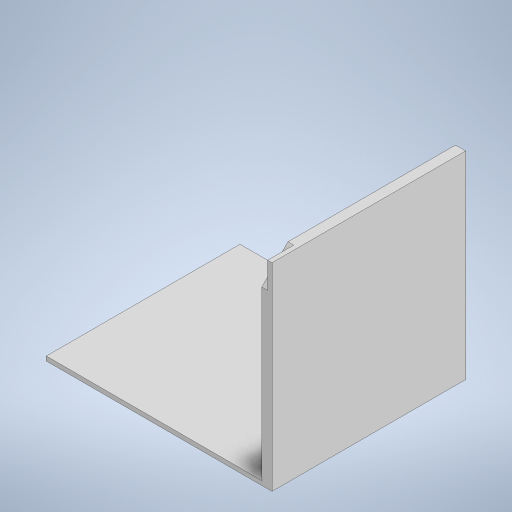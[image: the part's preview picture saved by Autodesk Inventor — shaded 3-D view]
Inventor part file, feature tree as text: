
AUTODESK INVENTOR PART (.ipt)
format: ipt  version: 2024 (Build 280153000, 153)  size: 322,048 bytes
history: native  units: mm
features: extrude x11, sketch x11
ambient origin geometry x8: Origin, YZ Plane, XZ Plane, XY Plane, X Axis, Y Axis, Z Axis, Center Point
bodies: Solid1 (feature_tree)
feature tree (22):
  extrude  "Top"  Depth=160.0mm
  extrude  "Right"  Depth=179.5mm
  extrude  "Left"  Depth=215.9mm
  extrude  "Plexiglass Cut"  Depth=25.4mm
  extrude  "Bottom"  Depth=266.7mm TaperAngle=0.0deg
  extrude  "Top Flattening"  Depth=266.7mm TaperAngle=0.0deg
  extrude  "Outer Side Flattening"  Depth=304.8mm TaperAngle=0.0deg
  extrude  "Bottom Flattening"  Depth=22.4mm TaperAngle=0.0deg
  extrude  "Inner Flattening"  Depth=22.389425mm
  extrude  "Top Cut"  Depth=22.4mm TaperAngle=0.0deg
  extrude  "Quarter Cut"  Depth=22.4mm TaperAngle=0.0deg
  sketch  "Sketch1"  dims[d11=220.0mm d12=160.0mm]
  sketch  "Sketch3"  dims[d15=248.6mm d16=179.5mm]
  sketch  "Sketch4"  dims[d18=304.8mm d19=215.9mm]
  sketch  "Sketch5"  dims[d20=25.4mm d21=0.0mm d22=25.4mm]
  sketch  "Sketch6"  dims[d25=266.7mm d26=50.8mm d27=0.0mm]
  sketch  "Sketch9"  dims[d28=266.7mm d29=50.8mm d30=0.0mm]
  sketch  "Sketch10"  dims[d31=12.7mm d32=304.8mm d33=0.0mm]
  sketch  "Sketch11"  dims[d34=25.4mm d35=0.0mm d46=22.4mm d47=0.0mm]
  sketch  "Sketch12"  dims[d48=22.389425mm d49=22.389425mm]
  sketch  "Sketch13"  dims[d50=0.0mm d51=0.0mm d52=22.4mm d53=0.0mm]
  sketch  "Sketch14"  dims[d54=296.8mm d55=22.4mm d56=0.0mm d57=0.0mm d58=0.0mm d59=0.0mm d60=0.0mm]
